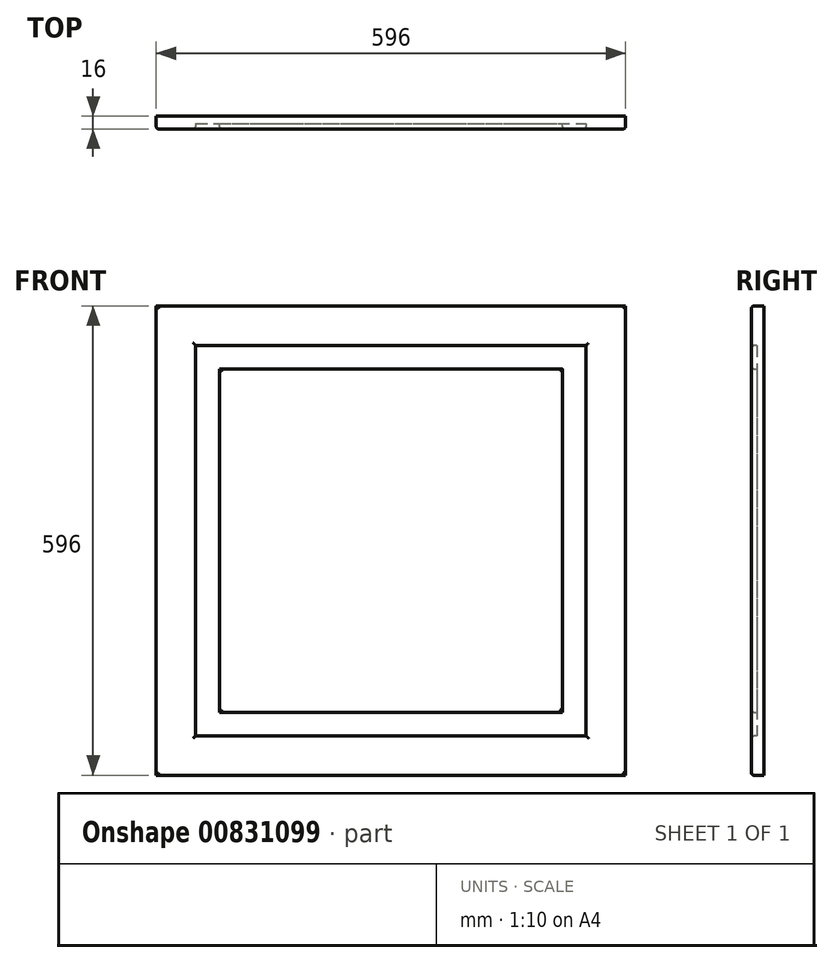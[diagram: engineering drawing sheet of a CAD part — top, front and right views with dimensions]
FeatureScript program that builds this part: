
annotation { "Feature Type Name" : "Feature", "Feature Type Description" : "" }
export const myFeature = defineFeature(function(context is Context, id is Id, definition is map)
    precondition{}
    {
        {
            var Q0;
            Q0=qCreatedBy(makeId("Front.planeOp"),FACE);
            var sketch = newSketch(context, id + "F0", { "sketchPlane" : qUnion([Q0])});
            skLineSegment(sketch, "E0.bottom", {"start": v(0, 0) * mm, "end": v(44.66, 0) * mm});
            skLineSegment(sketch, "E0.top", {"start": v(0, 33.8) * mm, "end": v(44.66, 33.8) * mm});
            skLineSegment(sketch, "E0.left", {"start": v(0, 0) * mm, "end": v(0, 33.8) * mm});
            skLineSegment(sketch, "E0.right", {"start": v(44.66, 0) * mm, "end": v(44.66, 33.8) * mm});
            skSolve(sketch);
        }
        {
            var Q0;
            Q0=makeQuery(id+"F0.imprint","IMPRINT",FACE,{"disambiguationData":[TD([[makeQuery(id+"F0.imprint","IMPRINT",EDGE,{"derivedFrom":sQuery(id+"F0.wireOp",EDGE,"E0.bottom")}),1.0]])]});
            extrude(context, id + "F1", {"entities" : qUnion([Q0]), "depth" : 16 * mm, "offsetDistance" : 25.4 * mm});
        }
        {
            var Q0;
            Q0=makeQuery(id+"F1.opExtrude","SWEPT_FACE",FACE,{"disambiguationData":[OSD([sQuery(id+"F0.wireOp",EDGE,"E0.bottom")])]});
            extrude(context, id + "F2", {"entities" : qUnion([Q0]), "operationType" : NewBodyOperationType.ADD, "oppositeDirection" : true, "depth" : 796 * mm, "offsetDistance" : 25 * mm});
        }
        {
            var Q0;
            {var subQ0=sQuery(id+"F0.wireOp",EDGE,"E0.left");Q0=makeQuery(id+"F2.boolean.opBoolean","MERGE",FACE,{"derivedFrom":[makeQuery(id+"F1.opExtrude","SWEPT_FACE",FACE,{"disambiguationData":[OSD([subQ0])]}),makeQuery(id+"F2.opExtrude","SWEPT_FACE",FACE,{"disambiguationData":[OSD([sQuery(id+"F0.wireOp",EDGE,"E0.bottom"),subQ0])]})]});}
            extrude(context, id + "F3", {"entities" : qUnion([Q0]), "operationType" : NewBodyOperationType.ADD, "oppositeDirection" : true, "depth" : 196 * mm, "offsetDistance" : 25 * mm});
        }
        {
            var Q0;
            {var subQ0=sQuery(id+"F0.wireOp",EDGE,"E0.left");var subQ1=sQuery(id+"F0.wireOp",EDGE,"E0.bottom");Q0=makeQuery(id+"F3.boolean.opBoolean","MERGE",FACE,{"derivedFrom":[makeQuery(id+"F2.boolean.opBoolean","MERGE",FACE,{"derivedFrom":[makeQuery(id+"F1.opExtrude","CAP_FACE",FACE,{"disambiguationData":[OSD([subQ1,sQuery(id+"F0.wireOp",EDGE,"E0.top"),subQ0,sQuery(id+"F0.wireOp",EDGE,"E0.right")])],"isStart":false}),makeQuery(id+"F2.opExtrude","SWEPT_FACE",FACE,{"disambiguationData":[OSD([subQ1]),TDD([makeQuery(id+"F1.opExtrude","CAP_EDGE",EDGE,{"disambiguationData":[OSD([subQ1])],"isStart":false})])]})]}),makeQuery(id+"F3.opExtrude","SWEPT_FACE",FACE,{"disambiguationData":[OSD([subQ1,subQ0]),TDD([makeQuery(id+"F2.boolean.opBoolean","MERGE",EDGE,{"derivedFrom":[makeQuery(id+"F1.opExtrude","CAP_EDGE",EDGE,{"disambiguationData":[OSD([subQ0])],"isStart":false}),makeQuery(id+"F2.opExtrude","SWEPT_EDGE",EDGE,{"disambiguationData":[OSD([subQ1,subQ0]),TDD([makeQuery(id+"F1.opExtrude","CAP_VERTEX",VERTEX,{"disambiguationData":[OSD([subQ1,subQ0])],"isStart":false})])]})]})])]})]});}
            var sketch = newSketch(context, id + "F4", { "sketchPlane" : qUnion([Q0])});
            skLineSegment(sketch, "E1.bottom", {"start": v(59.7, 646.67) * mm, "end": v(128.66, 646.67) * mm});
            skLineSegment(sketch, "E1.top", {"start": v(59.7, 152.97) * mm, "end": v(128.66, 152.97) * mm});
            skLineSegment(sketch, "E1.left", {"start": v(59.7, 646.67) * mm, "end": v(59.7, 152.97) * mm});
            skLineSegment(sketch, "E1.right", {"start": v(128.66, 646.67) * mm, "end": v(128.66, 152.97) * mm});
            skSolve(sketch);
        }
        {
            var Q0;
            Q0=makeQuery(id+"F4.imprint","IMPRINT",FACE,{"disambiguationData":[TD([[makeQuery(id+"F4.imprint","IMPRINT",EDGE,{"derivedFrom":sQuery(id+"F4.wireOp",EDGE,"E1.bottom")}),-1.0]])]});
            extrude(context, id + "F5", {"entities" : qUnion([Q0]), "operationType" : NewBodyOperationType.REMOVE, "oppositeDirection" : true, "depth" : 7 * mm, "offsetDistance" : 25 * mm});
        }
        {
            var Q0;
            Q0=makeQuery(id+"F5.boolean.opBoolean","COPY",FACE,{"derivedFrom":makeQuery(id+"F5.opExtrude","SWEPT_FACE",FACE,{"disambiguationData":[OSD([sQuery(id+"F4.wireOp",EDGE,"E1.left")])]})});
            extrude(context, id + "F6", {"entities" : qUnion([Q0]), "operationType" : NewBodyOperationType.REMOVE, "oppositeDirection" : true, "depth" : 9.7 * mm, "offsetDistance" : 25 * mm});
        }
        {
            var Q0;
            {var subQ0=sQuery(id+"F4.wireOp",EDGE,"E1.bottom");Q0=makeQuery(id+"F6.boolean.opBoolean","MERGE",FACE,{"derivedFrom":[makeQuery(id+"F5.boolean.opBoolean","COPY",FACE,{"derivedFrom":makeQuery(id+"F5.opExtrude","SWEPT_FACE",FACE,{"disambiguationData":[OSD([subQ0])]})}),makeQuery(id+"F6.opExtrude","SWEPT_FACE",FACE,{"disambiguationData":[OSD([subQ0,sQuery(id+"F4.wireOp",EDGE,"E1.left")])]})]});}
            extrude(context, id + "F7", {"entities" : qUnion([Q0]), "operationType" : NewBodyOperationType.ADD, "oppositeDirection" : true, "depth" : 99.33 * mm, "offsetDistance" : 25 * mm});
        }
        {
            var Q0;
            {var subQ0=sQuery(id+"F4.wireOp",EDGE,"E1.bottom");Q0=makeQuery(id+"F6.boolean.opBoolean","MERGE",FACE,{"derivedFrom":[makeQuery(id+"F5.boolean.opBoolean","COPY",FACE,{"derivedFrom":makeQuery(id+"F5.opExtrude","SWEPT_FACE",FACE,{"disambiguationData":[OSD([subQ0])]})}),makeQuery(id+"F6.opExtrude","SWEPT_FACE",FACE,{"disambiguationData":[OSD([subQ0,sQuery(id+"F4.wireOp",EDGE,"E1.left")])]})]});}
            extrude(context, id + "F8", {"entities" : qUnion([Q0]), "operationType" : NewBodyOperationType.REMOVE, "oppositeDirection" : true, "depth" : 99.33 * mm, "offsetDistance" : 25 * mm});
        }
        {
            var Q0;
            {var subQ0=sQuery(id+"F4.wireOp",EDGE,"E1.right");Q0=makeQuery(id+"F8.boolean.opBoolean","MERGE",FACE,{"derivedFrom":[makeQuery(id+"F5.boolean.opBoolean","COPY",FACE,{"derivedFrom":makeQuery(id+"F5.opExtrude","SWEPT_FACE",FACE,{"disambiguationData":[OSD([subQ0])]})}),makeQuery(id+"F8.opExtrude","SWEPT_FACE",FACE,{"disambiguationData":[OSD([sQuery(id+"F4.wireOp",EDGE,"E1.bottom"),subQ0])]})]});}
            extrude(context, id + "F9", {"entities" : qUnion([Q0]), "operationType" : NewBodyOperationType.REMOVE, "oppositeDirection" : true, "depth" : 17.34 * mm, "offsetDistance" : 25 * mm});
        }
        {
            var Q0;
            {var subQ0=sQuery(id+"F4.wireOp",EDGE,"E1.top");Q0=makeQuery(id+"F9.boolean.opBoolean","MERGE",FACE,{"derivedFrom":[makeQuery(id+"F6.boolean.opBoolean","MERGE",FACE,{"derivedFrom":[makeQuery(id+"F5.boolean.opBoolean","COPY",FACE,{"derivedFrom":makeQuery(id+"F5.opExtrude","SWEPT_FACE",FACE,{"disambiguationData":[OSD([subQ0])]})}),makeQuery(id+"F6.opExtrude","SWEPT_FACE",FACE,{"disambiguationData":[OSD([subQ0,sQuery(id+"F4.wireOp",EDGE,"E1.left")])]})]}),makeQuery(id+"F9.opExtrude","SWEPT_FACE",FACE,{"disambiguationData":[OSD([subQ0,sQuery(id+"F4.wireOp",EDGE,"E1.right")])]})]});}
            extrude(context, id + "F10", {"entities" : qUnion([Q0]), "operationType" : NewBodyOperationType.REMOVE, "oppositeDirection" : true, "depth" : 102.97 * mm, "offsetDistance" : 25 * mm});
        }
        {
            var Q0;
            {var subQ0=sQuery(id+"F4.wireOp",EDGE,"E1.right");var subQ1=sQuery(id+"F4.wireOp",EDGE,"E1.top");var subQ2=sQuery(id+"F4.wireOp",EDGE,"E1.left");var subQ3=sQuery(id+"F4.wireOp",EDGE,"E1.bottom");Q0=makeQuery(id+"F10.boolean.opBoolean","MERGE",FACE,{"derivedFrom":[makeQuery(id+"F9.boolean.opBoolean","MERGE",FACE,{"derivedFrom":[makeQuery(id+"F8.boolean.opBoolean","MERGE",FACE,{"derivedFrom":[makeQuery(id+"F6.boolean.opBoolean","MERGE",FACE,{"derivedFrom":[makeQuery(id+"F5.boolean.opBoolean","COPY",FACE,{"derivedFrom":makeQuery(id+"F5.opExtrude","CAP_FACE",FACE,{"disambiguationData":[OSD([subQ3,subQ1,subQ2,subQ0])],"isStart":false})}),makeQuery(id+"F6.opExtrude","SWEPT_FACE",FACE,{"disambiguationData":[OSD([subQ2]),TDD([makeQuery(id+"F5.boolean.opBoolean","COPY",EDGE,{"derivedFrom":makeQuery(id+"F5.opExtrude","CAP_EDGE",EDGE,{"disambiguationData":[OSD([subQ2])],"isStart":false})})])]})]}),makeQuery(id+"F8.opExtrude","SWEPT_FACE",FACE,{"disambiguationData":[OSD([subQ3,subQ2]),TDD([makeQuery(id+"F6.boolean.opBoolean","MERGE",EDGE,{"derivedFrom":[makeQuery(id+"F5.boolean.opBoolean","COPY",EDGE,{"derivedFrom":makeQuery(id+"F5.opExtrude","CAP_EDGE",EDGE,{"disambiguationData":[OSD([subQ3])],"isStart":false})}),makeQuery(id+"F6.opExtrude","SWEPT_EDGE",EDGE,{"disambiguationData":[OSD([subQ3,subQ2]),TDD([makeQuery(id+"F5.boolean.opBoolean","COPY",VERTEX,{"derivedFrom":makeQuery(id+"F5.opExtrude","CAP_VERTEX",VERTEX,{"disambiguationData":[OSD([subQ3,subQ2])],"isStart":false})})])]})]})])]})]}),makeQuery(id+"F9.opExtrude","SWEPT_FACE",FACE,{"disambiguationData":[OSD([subQ3,subQ0]),TDD([makeQuery(id+"F8.boolean.opBoolean","MERGE",EDGE,{"derivedFrom":[makeQuery(id+"F5.boolean.opBoolean","COPY",EDGE,{"derivedFrom":makeQuery(id+"F5.opExtrude","CAP_EDGE",EDGE,{"disambiguationData":[OSD([subQ0])],"isStart":false})}),makeQuery(id+"F8.opExtrude","SWEPT_EDGE",EDGE,{"disambiguationData":[OSD([subQ3,subQ0]),TDD([makeQuery(id+"F5.boolean.opBoolean","COPY",VERTEX,{"derivedFrom":makeQuery(id+"F5.opExtrude","CAP_VERTEX",VERTEX,{"disambiguationData":[OSD([subQ3,subQ0])],"isStart":false})})])]})]})])]})]}),makeQuery(id+"F10.opExtrude","SWEPT_FACE",FACE,{"disambiguationData":[OSD([subQ1,subQ2,subQ0]),TDD([makeQuery(id+"F9.boolean.opBoolean","MERGE",EDGE,{"derivedFrom":[makeQuery(id+"F6.boolean.opBoolean","MERGE",EDGE,{"derivedFrom":[makeQuery(id+"F5.boolean.opBoolean","COPY",EDGE,{"derivedFrom":makeQuery(id+"F5.opExtrude","CAP_EDGE",EDGE,{"disambiguationData":[OSD([subQ1])],"isStart":false})}),makeQuery(id+"F6.opExtrude","SWEPT_EDGE",EDGE,{"disambiguationData":[OSD([subQ1,subQ2]),TDD([makeQuery(id+"F5.boolean.opBoolean","COPY",VERTEX,{"derivedFrom":makeQuery(id+"F5.opExtrude","CAP_VERTEX",VERTEX,{"disambiguationData":[OSD([subQ1,subQ2])],"isStart":false})})])]})]}),makeQuery(id+"F9.opExtrude","SWEPT_EDGE",EDGE,{"disambiguationData":[OSD([subQ1,subQ0]),TDD([makeQuery(id+"F5.boolean.opBoolean","COPY",VERTEX,{"derivedFrom":makeQuery(id+"F5.opExtrude","CAP_VERTEX",VERTEX,{"disambiguationData":[OSD([subQ1,subQ0])],"isStart":false})})])]})]})])]})]});}
            var sketch = newSketch(context, id + "F11", { "sketchPlane" : qUnion([Q0])});
            skLineSegment(sketch, "E2.bottom", {"start": v(74.13, 678.73) * mm, "end": v(109.41, 678.73) * mm});
            skLineSegment(sketch, "E2.top", {"start": v(74.13, 186.63) * mm, "end": v(109.41, 186.63) * mm});
            skLineSegment(sketch, "E2.left", {"start": v(74.13, 678.73) * mm, "end": v(74.13, 186.63) * mm});
            skLineSegment(sketch, "E2.right", {"start": v(109.41, 678.73) * mm, "end": v(109.41, 186.63) * mm});
            skSolve(sketch);
        }
        {
            var Q0;
            Q0=makeQuery(id+"F11.imprint","IMPRINT",FACE,{"disambiguationData":[TD([[makeQuery(id+"F11.imprint","IMPRINT",EDGE,{"derivedFrom":sQuery(id+"F11.wireOp",EDGE,"E2.bottom")}),-1.0]])]});
            extrude(context, id + "F12", {"entities" : qUnion([Q0]), "operationType" : NewBodyOperationType.ADD, "depth" : 7 * mm, "offsetDistance" : 25 * mm});
        }
        {
            var Q0;
            Q0=makeQuery(id+"F12.opExtrude","SWEPT_FACE",FACE,{"disambiguationData":[OSD([sQuery(id+"F11.wireOp",EDGE,"E2.bottom")])]});
            extrude(context, id + "F13", {"entities" : qUnion([Q0]), "operationType" : NewBodyOperationType.ADD, "depth" : 37.27 * mm, "offsetDistance" : 25 * mm});
        }
        {
            var Q0;
            {var subQ0=sQuery(id+"F11.wireOp",EDGE,"E2.right");Q0=makeQuery(id+"F13.boolean.opBoolean","MERGE",FACE,{"derivedFrom":[makeQuery(id+"F12.opExtrude","SWEPT_FACE",FACE,{"disambiguationData":[OSD([subQ0])]}),makeQuery(id+"F13.opExtrude","SWEPT_FACE",FACE,{"disambiguationData":[OSD([sQuery(id+"F11.wireOp",EDGE,"E2.bottom"),subQ0])]})]});}
            extrude(context, id + "F14", {"entities" : qUnion([Q0]), "operationType" : NewBodyOperationType.ADD, "depth" : 6.58 * mm, "offsetDistance" : 25 * mm});
        }
        {
            var Q0;
            {var subQ0=sQuery(id+"F11.wireOp",EDGE,"E2.top");Q0=makeQuery(id+"F14.boolean.opBoolean","MERGE",FACE,{"derivedFrom":[makeQuery(id+"F12.opExtrude","SWEPT_FACE",FACE,{"disambiguationData":[OSD([subQ0])]}),makeQuery(id+"F14.opExtrude","SWEPT_FACE",FACE,{"disambiguationData":[OSD([subQ0,sQuery(id+"F11.wireOp",EDGE,"E2.right")])]})]});}
            extrude(context, id + "F15", {"entities" : qUnion([Q0]), "operationType" : NewBodyOperationType.ADD, "depth" : 106.63 * mm, "offsetDistance" : 25 * mm});
        }
        {
            var Q0;
            {var subQ0=sQuery(id+"F11.wireOp",EDGE,"E2.left");Q0=makeQuery(id+"F15.boolean.opBoolean","MERGE",FACE,{"derivedFrom":[makeQuery(id+"F13.boolean.opBoolean","MERGE",FACE,{"derivedFrom":[makeQuery(id+"F12.opExtrude","SWEPT_FACE",FACE,{"disambiguationData":[OSD([subQ0])]}),makeQuery(id+"F13.opExtrude","SWEPT_FACE",FACE,{"disambiguationData":[OSD([sQuery(id+"F11.wireOp",EDGE,"E2.bottom"),subQ0])]})]}),makeQuery(id+"F15.opExtrude","SWEPT_FACE",FACE,{"disambiguationData":[OSD([sQuery(id+"F11.wireOp",EDGE,"E2.top"),subQ0])]})]});}
            extrude(context, id + "F16", {"entities" : qUnion([Q0]), "operationType" : NewBodyOperationType.REMOVE, "oppositeDirection" : true, "depth" : 5.87 * mm, "offsetDistance" : 25 * mm});
        }
        {
            var Q0;
            Q0=makeQuery(id+"F3.opExtrude","CAP_FACE",FACE,{"disambiguationData":[OSD([sQuery(id+"F0.wireOp",EDGE,"E0.bottom"),sQuery(id+"F0.wireOp",EDGE,"E0.left")])],"isStart":false});
            extrude(context, id + "F17", {"entities" : qUnion([Q0]), "operationType" : NewBodyOperationType.ADD, "depth" : 200 * mm, "offsetDistance" : 25 * mm});
        }
        {
            var Q0;
            {var subQ0=sQuery(id+"F4.wireOp",EDGE,"E1.right");Q0=makeQuery(id+"F10.boolean.opBoolean","MERGE",FACE,{"derivedFrom":[makeQuery(id+"F9.boolean.opBoolean","COPY",FACE,{"derivedFrom":makeQuery(id+"F9.opExtrude","CAP_FACE",FACE,{"disambiguationData":[OSD([sQuery(id+"F4.wireOp",EDGE,"E1.bottom"),subQ0])],"isStart":false})}),makeQuery(id+"F10.opExtrude","SWEPT_FACE",FACE,{"disambiguationData":[OSD([sQuery(id+"F4.wireOp",EDGE,"E1.top"),subQ0])]})]});}
            extrude(context, id + "F18", {"entities" : qUnion([Q0]), "operationType" : NewBodyOperationType.REMOVE, "oppositeDirection" : true, "depth" : 200 * mm, "offsetDistance" : 25 * mm});
        }
        {
            var Q0;
            {var subQ0=sQuery(id+"F11.wireOp",EDGE,"E2.right");var subQ1=sQuery(id+"F11.wireOp",EDGE,"E2.top");Q0=makeQuery(id+"F15.boolean.opBoolean","MERGE",FACE,{"derivedFrom":[makeQuery(id+"F14.opExtrude","CAP_FACE",FACE,{"disambiguationData":[OSD([sQuery(id+"F11.wireOp",EDGE,"E2.bottom"),subQ0])],"isStart":false}),makeQuery(id+"F15.opExtrude","SWEPT_FACE",FACE,{"disambiguationData":[OSD([subQ1,subQ0]),TDD([makeQuery(id+"F14.opExtrude","CAP_EDGE",EDGE,{"disambiguationData":[OSD([subQ1,subQ0])],"isStart":false})])]})]});}
            extrude(context, id + "F19", {"entities" : qUnion([Q0]), "operationType" : NewBodyOperationType.ADD, "depth" : 200 * mm, "offsetDistance" : 25 * mm});
        }
        {
            var Q0;
            Q0=makeQuery(id+"F17.opExtrude","CAP_FACE",FACE,{"disambiguationData":[OSD([sQuery(id+"F0.wireOp",EDGE,"E0.bottom"),sQuery(id+"F0.wireOp",EDGE,"E0.left")])],"isStart":false});
            extrude(context, id + "F20", {"entities" : qUnion([Q0]), "operationType" : NewBodyOperationType.ADD, "depth" : 200 * mm, "offsetDistance" : 25 * mm});
        }
        {
            var Q0;
            Q0=makeQuery(id+"F18.boolean.opBoolean","COPY",FACE,{"derivedFrom":makeQuery(id+"F18.opExtrude","CAP_FACE",FACE,{"disambiguationData":[OSD([sQuery(id+"F4.wireOp",EDGE,"E1.bottom"),sQuery(id+"F4.wireOp",EDGE,"E1.top"),sQuery(id+"F4.wireOp",EDGE,"E1.right")])],"isStart":false})});
            extrude(context, id + "F21", {"entities" : qUnion([Q0]), "operationType" : NewBodyOperationType.REMOVE, "oppositeDirection" : true, "depth" : 200 * mm, "offsetDistance" : 25 * mm});
        }
        {
            var Q0;
            Q0=makeQuery(id+"F19.opExtrude","CAP_FACE",FACE,{"disambiguationData":[OSD([sQuery(id+"F11.wireOp",EDGE,"E2.bottom"),sQuery(id+"F11.wireOp",EDGE,"E2.top"),sQuery(id+"F11.wireOp",EDGE,"E2.right")])],"isStart":false});
            extrude(context, id + "F22", {"entities" : qUnion([Q0]), "operationType" : NewBodyOperationType.ADD, "depth" : 200 * mm, "offsetDistance" : 25 * mm});
        }
        {
            var Q0;
            {var subQ0=sQuery(id+"F11.wireOp",EDGE,"E2.right");var subQ1=sQuery(id+"F11.wireOp",EDGE,"E2.bottom");Q0=makeQuery(id+"F22.boolean.opBoolean","MERGE",FACE,{"derivedFrom":[makeQuery(id+"F19.boolean.opBoolean","MERGE",FACE,{"derivedFrom":[makeQuery(id+"F14.boolean.opBoolean","MERGE",FACE,{"derivedFrom":[makeQuery(id+"F13.opExtrude","CAP_FACE",FACE,{"disambiguationData":[OSD([subQ1])],"isStart":false}),makeQuery(id+"F14.opExtrude","SWEPT_FACE",FACE,{"disambiguationData":[OSD([subQ1,subQ0]),TDD([makeQuery(id+"F13.opExtrude","CAP_EDGE",EDGE,{"disambiguationData":[OSD([subQ1,subQ0])],"isStart":false})])]})]}),makeQuery(id+"F19.opExtrude","SWEPT_FACE",FACE,{"disambiguationData":[OSD([subQ1,subQ0])]})]}),makeQuery(id+"F22.opExtrude","SWEPT_FACE",FACE,{"disambiguationData":[OSD([subQ1,subQ0])]})]});}
            extrude(context, id + "F23", {"entities" : qUnion([Q0]), "operationType" : NewBodyOperationType.REMOVE, "oppositeDirection" : true, "depth" : 200 * mm, "offsetDistance" : 25 * mm});
        }
        {
            var Q0;
            {var subQ0=sQuery(id+"F4.wireOp",EDGE,"E1.right");var subQ1=sQuery(id+"F4.wireOp",EDGE,"E1.bottom");Q0=makeQuery(id+"F21.boolean.opBoolean","MERGE",FACE,{"derivedFrom":[makeQuery(id+"F18.boolean.opBoolean","MERGE",FACE,{"derivedFrom":[makeQuery(id+"F9.boolean.opBoolean","MERGE",FACE,{"derivedFrom":[makeQuery(id+"F8.boolean.opBoolean","COPY",FACE,{"derivedFrom":makeQuery(id+"F8.opExtrude","CAP_FACE",FACE,{"disambiguationData":[OSD([subQ1,sQuery(id+"F4.wireOp",EDGE,"E1.left")])],"isStart":false})}),makeQuery(id+"F9.opExtrude","SWEPT_FACE",FACE,{"disambiguationData":[OSD([subQ1,subQ0]),TDD([makeQuery(id+"F8.boolean.opBoolean","COPY",EDGE,{"derivedFrom":makeQuery(id+"F8.opExtrude","CAP_EDGE",EDGE,{"disambiguationData":[OSD([subQ1,subQ0])],"isStart":false})})])]})]}),makeQuery(id+"F18.opExtrude","SWEPT_FACE",FACE,{"disambiguationData":[OSD([subQ1,subQ0])]})]}),makeQuery(id+"F21.opExtrude","SWEPT_FACE",FACE,{"disambiguationData":[OSD([subQ1,subQ0])]})]});}
            extrude(context, id + "F24", {"entities" : qUnion([Q0]), "operationType" : NewBodyOperationType.ADD, "depth" : 200 * mm, "offsetDistance" : 25 * mm});
        }
        {
            var Q0;
            {var subQ0=sQuery(id+"F0.wireOp",EDGE,"E0.left");var subQ1=sQuery(id+"F0.wireOp",EDGE,"E0.bottom");var subQ2=makeQuery(id+"F2.opExtrude","CAP_EDGE",EDGE,{"disambiguationData":[OSD([subQ1,subQ0])],"isStart":false});var subQ3=makeQuery(id+"F3.opExtrude","CAP_EDGE",EDGE,{"disambiguationData":[OSD([subQ1,subQ0]),TDD([subQ2])],"isStart":false});Q0=makeQuery(id+"F20.boolean.opBoolean","MERGE",FACE,{"derivedFrom":[makeQuery(id+"F17.boolean.opBoolean","MERGE",FACE,{"derivedFrom":[makeQuery(id+"F3.boolean.opBoolean","MERGE",FACE,{"derivedFrom":[makeQuery(id+"F2.opExtrude","CAP_FACE",FACE,{"disambiguationData":[OSD([subQ1])],"isStart":false}),makeQuery(id+"F3.opExtrude","SWEPT_FACE",FACE,{"disambiguationData":[OSD([subQ1,subQ0]),TDD([subQ2])]})]}),makeQuery(id+"F17.opExtrude","SWEPT_FACE",FACE,{"disambiguationData":[OSD([subQ1,subQ0]),TDD([subQ3])]})]}),makeQuery(id+"F20.opExtrude","SWEPT_FACE",FACE,{"disambiguationData":[OSD([subQ1,subQ0]),TDD([makeQuery(id+"F17.opExtrude","CAP_EDGE",EDGE,{"disambiguationData":[OSD([subQ1,subQ0]),TDD([subQ3])],"isStart":false})])]})]});}
            extrude(context, id + "F25", {"entities" : qUnion([Q0]), "operationType" : NewBodyOperationType.REMOVE, "oppositeDirection" : true, "depth" : 200 * mm, "offsetDistance" : 25 * mm});
        }
        {
            var Q0;
            {var subQ0=sQuery(id+"F4.wireOp",EDGE,"E1.right");var subQ1=sQuery(id+"F4.wireOp",EDGE,"E1.bottom");var subQ2=makeQuery(id+"F8.boolean.opBoolean","COPY",VERTEX,{"derivedFrom":makeQuery(id+"F8.opExtrude","CAP_VERTEX",VERTEX,{"disambiguationData":[OSD([subQ1,subQ0]),TDD([makeQuery(id+"F5.boolean.opBoolean","COPY",VERTEX,{"derivedFrom":makeQuery(id+"F5.opExtrude","CAP_VERTEX",VERTEX,{"disambiguationData":[OSD([subQ1,subQ0])],"isStart":true})})])],"isStart":false})});var subQ3=makeQuery(id+"F9.boolean.opBoolean","COPY",VERTEX,{"derivedFrom":makeQuery(id+"F9.opExtrude","CAP_VERTEX",VERTEX,{"disambiguationData":[OSD([subQ1,subQ0]),TDD([subQ2])],"isStart":false})});var subQ4=sQuery(id+"F4.wireOp",EDGE,"E1.left");var subQ5=sQuery(id+"F0.wireOp",EDGE,"E0.left");var subQ6=sQuery(id+"F0.wireOp",EDGE,"E0.bottom");var subQ7=makeQuery(id+"F2.boolean.opBoolean","MERGE",EDGE,{"derivedFrom":[makeQuery(id+"F1.opExtrude","CAP_EDGE",EDGE,{"disambiguationData":[OSD([subQ5])],"isStart":false}),makeQuery(id+"F2.opExtrude","SWEPT_EDGE",EDGE,{"disambiguationData":[OSD([subQ6,subQ5]),TDD([makeQuery(id+"F1.opExtrude","CAP_VERTEX",VERTEX,{"disambiguationData":[OSD([subQ6,subQ5])],"isStart":false})])]})]});var subQ8=makeQuery(id+"F3.opExtrude","CAP_EDGE",EDGE,{"disambiguationData":[OSD([subQ6,subQ5]),TDD([subQ7])],"isStart":false});Q0=makeQuery(id+"F24.boolean.opBoolean","MERGE",FACE,{"derivedFrom":[makeQuery(id+"F20.boolean.opBoolean","MERGE",FACE,{"derivedFrom":[makeQuery(id+"F17.boolean.opBoolean","MERGE",FACE,{"derivedFrom":[makeQuery(id+"F3.boolean.opBoolean","MERGE",FACE,{"derivedFrom":[makeQuery(id+"F2.boolean.opBoolean","MERGE",FACE,{"derivedFrom":[makeQuery(id+"F1.opExtrude","CAP_FACE",FACE,{"disambiguationData":[OSD([subQ6,sQuery(id+"F0.wireOp",EDGE,"E0.top"),subQ5,sQuery(id+"F0.wireOp",EDGE,"E0.right")])],"isStart":false}),makeQuery(id+"F2.opExtrude","SWEPT_FACE",FACE,{"disambiguationData":[OSD([subQ6]),TDD([makeQuery(id+"F1.opExtrude","CAP_EDGE",EDGE,{"disambiguationData":[OSD([subQ6])],"isStart":false})])]})]}),makeQuery(id+"F3.opExtrude","SWEPT_FACE",FACE,{"disambiguationData":[OSD([subQ6,subQ5]),TDD([subQ7])]})]}),makeQuery(id+"F17.opExtrude","SWEPT_FACE",FACE,{"disambiguationData":[OSD([subQ6,subQ5]),TDD([subQ8])]})]}),makeQuery(id+"F20.opExtrude","SWEPT_FACE",FACE,{"disambiguationData":[OSD([subQ6,subQ5]),TDD([makeQuery(id+"F17.opExtrude","CAP_EDGE",EDGE,{"disambiguationData":[OSD([subQ6,subQ5]),TDD([subQ8])],"isStart":false})])]})]}),makeQuery(id+"F24.opExtrude","SWEPT_FACE",FACE,{"disambiguationData":[OSD([subQ1,subQ4,subQ0]),TDD([makeQuery(id+"F21.boolean.opBoolean","MERGE",EDGE,{"derivedFrom":[makeQuery(id+"F18.boolean.opBoolean","MERGE",EDGE,{"derivedFrom":[makeQuery(id+"F9.boolean.opBoolean","MERGE",EDGE,{"derivedFrom":[makeQuery(id+"F8.boolean.opBoolean","COPY",EDGE,{"derivedFrom":makeQuery(id+"F8.opExtrude","CAP_EDGE",EDGE,{"disambiguationData":[OSD([subQ1,subQ4]),TDD([makeQuery(id+"F6.boolean.opBoolean","MERGE",EDGE,{"derivedFrom":[makeQuery(id+"F5.boolean.opBoolean","COPY",EDGE,{"derivedFrom":makeQuery(id+"F5.opExtrude","CAP_EDGE",EDGE,{"disambiguationData":[OSD([subQ1])],"isStart":true})}),makeQuery(id+"F6.opExtrude","SWEPT_EDGE",EDGE,{"disambiguationData":[OSD([subQ1,subQ4]),TDD([makeQuery(id+"F5.boolean.opBoolean","COPY",VERTEX,{"derivedFrom":makeQuery(id+"F5.opExtrude","CAP_VERTEX",VERTEX,{"disambiguationData":[OSD([subQ1,subQ4])],"isStart":true})})])]})]})])],"isStart":false})}),makeQuery(id+"F9.opExtrude","SWEPT_EDGE",EDGE,{"disambiguationData":[OSD([subQ1,subQ0]),TDD([subQ2])]})]}),makeQuery(id+"F18.opExtrude","SWEPT_EDGE",EDGE,{"disambiguationData":[OSD([subQ1,subQ0]),TDD([subQ3])]})]}),makeQuery(id+"F21.opExtrude","SWEPT_EDGE",EDGE,{"disambiguationData":[OSD([subQ1,subQ0]),TDD([makeQuery(id+"F18.boolean.opBoolean","COPY",VERTEX,{"derivedFrom":makeQuery(id+"F18.opExtrude","CAP_VERTEX",VERTEX,{"disambiguationData":[OSD([subQ1,subQ0]),TDD([subQ3])],"isStart":false})})])]})]})])]})]});}
            var Q1;
            {var subQ0=sQuery(id+"F11.wireOp",EDGE,"E2.right");var subQ1=sQuery(id+"F11.wireOp",EDGE,"E2.top");var subQ2=makeQuery(id+"F12.opExtrude","CAP_VERTEX",VERTEX,{"disambiguationData":[OSD([subQ1,subQ0])],"isStart":false});var subQ3=sQuery(id+"F11.wireOp",EDGE,"E2.bottom");var subQ4=makeQuery(id+"F13.boolean.opBoolean","MERGE",EDGE,{"derivedFrom":[makeQuery(id+"F12.opExtrude","CAP_EDGE",EDGE,{"disambiguationData":[OSD([subQ0])],"isStart":false}),makeQuery(id+"F13.opExtrude","SWEPT_EDGE",EDGE,{"disambiguationData":[OSD([subQ3,subQ0]),TDD([makeQuery(id+"F12.opExtrude","CAP_VERTEX",VERTEX,{"disambiguationData":[OSD([subQ3,subQ0])],"isStart":false})])]})]});var subQ5=makeQuery(id+"F15.boolean.opBoolean","MERGE",EDGE,{"derivedFrom":[makeQuery(id+"F14.opExtrude","CAP_EDGE",EDGE,{"disambiguationData":[OSD([subQ3,subQ0]),TDD([subQ4])],"isStart":false}),makeQuery(id+"F15.opExtrude","SWEPT_EDGE",EDGE,{"disambiguationData":[OSD([subQ1,subQ0]),TDD([makeQuery(id+"F14.opExtrude","CAP_VERTEX",VERTEX,{"disambiguationData":[OSD([subQ1,subQ0]),TDD([subQ2])],"isStart":false})])]})]});Q1=makeQuery(id+"F22.boolean.opBoolean","MERGE",FACE,{"derivedFrom":[makeQuery(id+"F19.boolean.opBoolean","MERGE",FACE,{"derivedFrom":[makeQuery(id+"F15.boolean.opBoolean","MERGE",FACE,{"derivedFrom":[makeQuery(id+"F14.boolean.opBoolean","MERGE",FACE,{"derivedFrom":[makeQuery(id+"F13.boolean.opBoolean","MERGE",FACE,{"derivedFrom":[makeQuery(id+"F12.opExtrude","CAP_FACE",FACE,{"disambiguationData":[OSD([subQ3,subQ1,sQuery(id+"F11.wireOp",EDGE,"E2.left"),subQ0])],"isStart":false}),makeQuery(id+"F13.opExtrude","SWEPT_FACE",FACE,{"disambiguationData":[OSD([subQ3]),TDD([makeQuery(id+"F12.opExtrude","CAP_EDGE",EDGE,{"disambiguationData":[OSD([subQ3])],"isStart":false})])]})]}),makeQuery(id+"F14.opExtrude","SWEPT_FACE",FACE,{"disambiguationData":[OSD([subQ3,subQ0]),TDD([subQ4])]})]}),makeQuery(id+"F15.opExtrude","SWEPT_FACE",FACE,{"disambiguationData":[OSD([subQ1,subQ0]),TDD([makeQuery(id+"F14.boolean.opBoolean","MERGE",EDGE,{"derivedFrom":[makeQuery(id+"F12.opExtrude","CAP_EDGE",EDGE,{"disambiguationData":[OSD([subQ1])],"isStart":false}),makeQuery(id+"F14.opExtrude","SWEPT_EDGE",EDGE,{"disambiguationData":[OSD([subQ1,subQ0]),TDD([subQ2])]})]})])]})]}),makeQuery(id+"F19.opExtrude","SWEPT_FACE",FACE,{"disambiguationData":[OSD([subQ3,subQ1,subQ0]),TDD([subQ5])]})]}),makeQuery(id+"F22.opExtrude","SWEPT_FACE",FACE,{"disambiguationData":[OSD([subQ3,subQ1,subQ0]),TDD([makeQuery(id+"F19.opExtrude","CAP_EDGE",EDGE,{"disambiguationData":[OSD([subQ3,subQ1,subQ0]),TDD([subQ5])],"isStart":false})])]})]});}
            fillet(context, id + "F26", {"entities" : qUnion([Q0, Q1]), "radius" : 3 * mm, "tangentPropagation" : true, "allowEdgeOverflow" : false});
        }
    });
